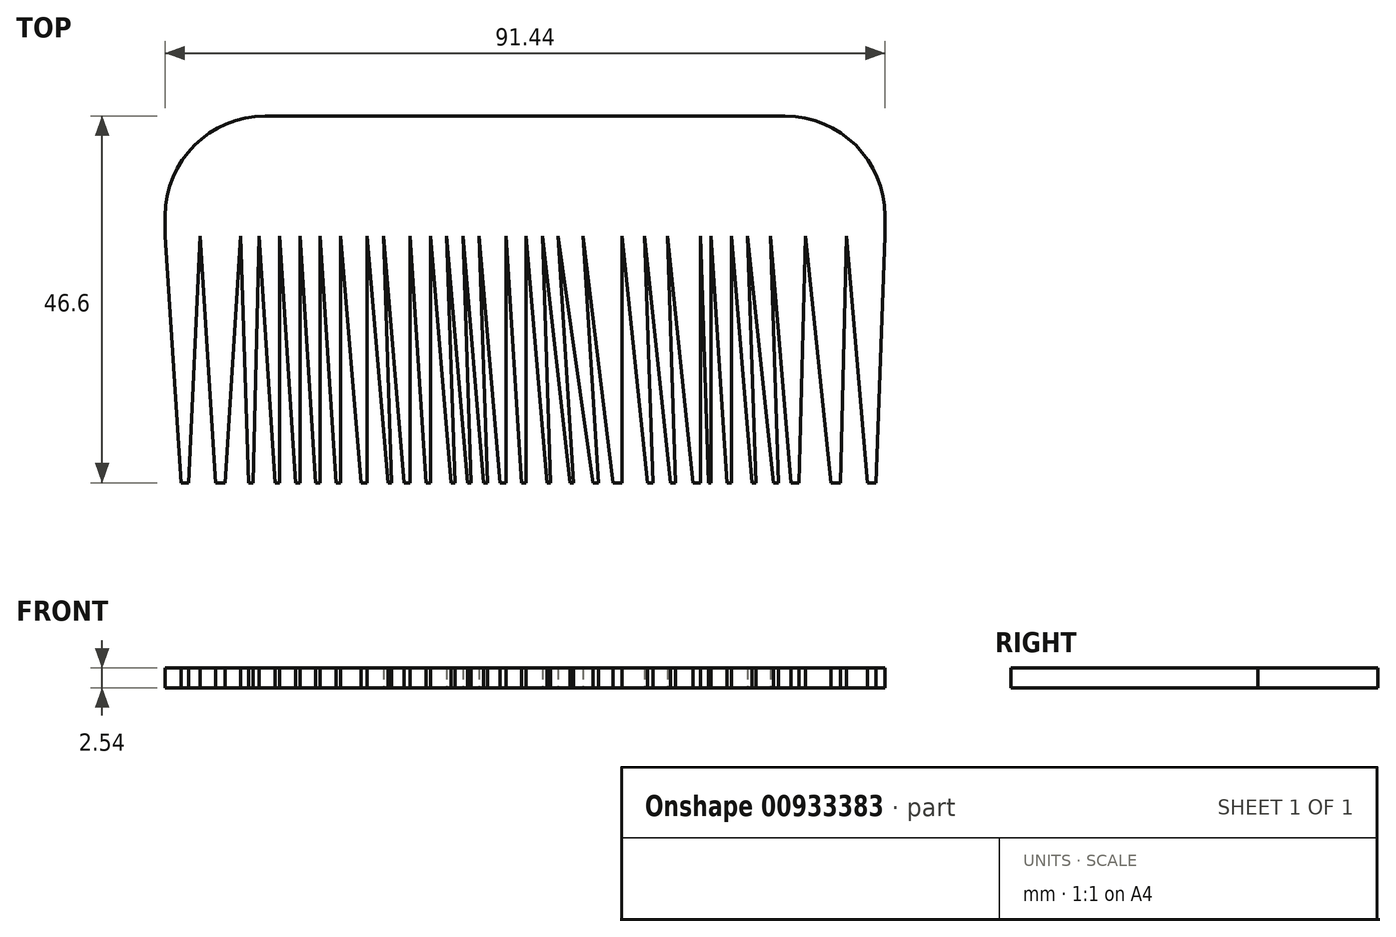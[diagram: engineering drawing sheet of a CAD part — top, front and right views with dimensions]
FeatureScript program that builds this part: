
annotation { "Feature Type Name" : "Feature", "Feature Type Description" : "" }
export const myFeature = defineFeature(function(context is Context, id is Id, definition is map)
    precondition{}
    {
        {
            var Q0;
            Q0=qCreatedBy(makeId("Top.planeOp"),FACE);
            var sketch = newSketch(context, id + "F0", { "sketchPlane" : qUnion([Q0])});
            skLineSegment(sketch, "E0.bottom", {"start": v(-18.06, 9.44) * mm, "end": v(73.38, 9.44) * mm});
            skLineSegment(sketch, "E0.top", {"start": v(-18.06, -5.8) * mm, "end": v(73.38, -5.8) * mm});
            skLineSegment(sketch, "E0.left", {"start": v(-18.06, 9.44) * mm, "end": v(-18.06, -5.8) * mm});
            skLineSegment(sketch, "E0.right", {"start": v(73.38, 9.44) * mm, "end": v(73.38, -5.8) * mm});
            skLineSegment(sketch, "E1", {"start": v(-18.06, -5.8) * mm, "end": v(-15.48, -46.4) * mm});
            skLineSegment(sketch, "E2", {"start": v(-15.48, -46.4) * mm, "end": v(73.76, -46.4) * mm});
            skLineSegment(sketch, "E3", {"start": v(-15.48, -46.4) * mm, "end": v(-13.62, -5.8) * mm});
            skLineSegment(sketch, "E4", {"start": v(-13.62, -5.8) * mm, "end": v(-11.04, -46.4) * mm});
            skLineSegment(sketch, "E5", {"start": v(-11.04, -46.4) * mm, "end": v(-8.47, -5.8) * mm});
            skLineSegment(sketch, "E6", {"start": v(-8.47, -5.8) * mm, "end": v(-7.13, -46.4) * mm});
            skLineSegment(sketch, "E7", {"start": v(-7.13, -46.4) * mm, "end": v(-6.1, -5.8) * mm});
            skLineSegment(sketch, "E8", {"start": v(-6.1, -5.8) * mm, "end": v(-3.52, -46.4) * mm});
            skLineSegment(sketch, "E9", {"start": v(-3.52, -46.4) * mm, "end": v(-3.52, -5.8) * mm});
            skLineSegment(sketch, "E10", {"start": v(-3.52, -5.8) * mm, "end": v(-0.94, -46.4) * mm});
            skLineSegment(sketch, "E11", {"start": v(-0.94, -46.4) * mm, "end": v(-0.94, -5.8) * mm});
            skLineSegment(sketch, "E12", {"start": v(-0.94, -5.8) * mm, "end": v(1.64, -46.4) * mm});
            skLineSegment(sketch, "E13", {"start": v(1.64, -46.4) * mm, "end": v(1.64, -5.8) * mm});
            skLineSegment(sketch, "E14", {"start": v(1.64, -5.8) * mm, "end": v(4.2, -46.2) * mm});
            skLineSegment(sketch, "E15", {"start": v(4.2, -46.2) * mm, "end": v(4.2, -5.8) * mm});
            skLineSegment(sketch, "E16", {"start": v(4.2, -5.8) * mm, "end": v(7.6, -46.4) * mm});
            skLineSegment(sketch, "E17", {"start": v(7.6, -46.4) * mm, "end": v(7.6, -5.8) * mm});
            skLineSegment(sketch, "E18", {"start": v(7.6, -5.8) * mm, "end": v(11, -46.4) * mm});
            skLineSegment(sketch, "E19", {"start": v(11, -46.4) * mm, "end": v(9.67, -5.8) * mm});
            skLineSegment(sketch, "E20", {"start": v(9.67, -5.8) * mm, "end": v(13.07, -46.4) * mm});
            skLineSegment(sketch, "E21", {"start": v(13.07, -46.4) * mm, "end": v(13.07, -5.8) * mm});
            skLineSegment(sketch, "E22", {"start": v(13.07, -5.8) * mm, "end": v(15.65, -46.4) * mm});
            skLineSegment(sketch, "E23", {"start": v(15.65, -46.4) * mm, "end": v(15.65, -5.8) * mm});
            skLineSegment(sketch, "E24", {"start": v(15.65, -5.8) * mm, "end": v(19.05, -46.4) * mm});
            skLineSegment(sketch, "E25", {"start": v(19.05, -46.4) * mm, "end": v(17.7, -5.8) * mm});
            skLineSegment(sketch, "E26", {"start": v(17.7, -5.8) * mm, "end": v(21.1, -46.4) * mm});
            skLineSegment(sketch, "E27", {"start": v(21.1, -46.4) * mm, "end": v(19.77, -5.8) * mm});
            skLineSegment(sketch, "E28", {"start": v(19.77, -5.8) * mm, "end": v(23.17, -46.4) * mm});
            skLineSegment(sketch, "E29", {"start": v(23.17, -46.4) * mm, "end": v(21.83, -5.8) * mm});
            skLineSegment(sketch, "E30", {"start": v(21.83, -5.8) * mm, "end": v(25.23, -46.4) * mm});
            skLineSegment(sketch, "E31", {"start": v(25.23, -46.4) * mm, "end": v(25.23, -5.8) * mm});
            skLineSegment(sketch, "E32", {"start": v(25.23, -5.8) * mm, "end": v(27.81, -46.4) * mm});
            skLineSegment(sketch, "E33", {"start": v(27.81, -46.4) * mm, "end": v(27.81, -5.8) * mm});
            skLineSegment(sketch, "E34", {"start": v(27.81, -5.8) * mm, "end": v(31.21, -46.4) * mm});
            skLineSegment(sketch, "E35", {"start": v(31.21, -46.4) * mm, "end": v(29.87, -5.8) * mm});
            skLineSegment(sketch, "E36", {"start": v(29.87, -5.8) * mm, "end": v(34.4, -46.4) * mm});
            skLineSegment(sketch, "E37", {"start": v(34.4, -46.4) * mm, "end": v(31.82, -5.8) * mm});
            skLineSegment(sketch, "E38", {"start": v(31.82, -5.8) * mm, "end": v(37.6, -46.4) * mm});
            skLineSegment(sketch, "E39", {"start": v(37.6, -46.4) * mm, "end": v(35.01, -5.8) * mm});
            skLineSegment(sketch, "E40", {"start": v(35.01, -5.8) * mm, "end": v(39.96, -46.4) * mm});
            skLineSegment(sketch, "E41", {"start": v(39.96, -46.4) * mm, "end": v(39.96, -5.8) * mm});
            skLineSegment(sketch, "E42", {"start": v(39.96, -5.8) * mm, "end": v(44.19, -46.4) * mm});
            skLineSegment(sketch, "E43", {"start": v(44.19, -46.4) * mm, "end": v(42.85, -5.8) * mm});
            skLineSegment(sketch, "E44", {"start": v(42.85, -5.8) * mm, "end": v(47.07, -46.4) * mm});
            skLineSegment(sketch, "E45", {"start": v(47.07, -46.4) * mm, "end": v(45.73, -5.8) * mm});
            skLineSegment(sketch, "E46", {"start": v(45.73, -5.8) * mm, "end": v(49.96, -46.4) * mm});
            skLineSegment(sketch, "E47", {"start": v(49.96, -46.4) * mm, "end": v(49.96, -5.8) * mm});
            skLineSegment(sketch, "E48", {"start": v(49.96, -5.8) * mm, "end": v(51.3, -46.4) * mm});
            skLineSegment(sketch, "E49", {"start": v(51.3, -46.4) * mm, "end": v(51.3, -5.8) * mm});
            skLineSegment(sketch, "E50", {"start": v(51.3, -5.8) * mm, "end": v(53.88, -46.4) * mm});
            skLineSegment(sketch, "E51", {"start": v(53.88, -46.4) * mm, "end": v(53.88, -5.8) * mm});
            skLineSegment(sketch, "E52", {"start": v(53.88, -5.8) * mm, "end": v(57.28, -46.4) * mm});
            skLineSegment(sketch, "E53", {"start": v(57.28, -46.4) * mm, "end": v(55.94, -5.8) * mm});
            skLineSegment(sketch, "E54", {"start": v(55.94, -5.8) * mm, "end": v(60.16, -46.4) * mm});
            skLineSegment(sketch, "E55", {"start": v(60.16, -46.4) * mm, "end": v(58.82, -5.8) * mm});
            skLineSegment(sketch, "E56", {"start": v(58.82, -5.8) * mm, "end": v(62.22, -46.4) * mm});
            skLineSegment(sketch, "E57", {"start": v(62.22, -46.4) * mm, "end": v(63.25, -5.8) * mm});
            skLineSegment(sketch, "E58", {"start": v(63.25, -5.8) * mm, "end": v(67.48, -46.4) * mm});
            skLineSegment(sketch, "E59", {"start": v(67.48, -46.4) * mm, "end": v(68.51, -5.8) * mm});
            skLineSegment(sketch, "E60", {"start": v(68.51, -5.8) * mm, "end": v(71.91, -46.4) * mm});
            skLineSegment(sketch, "E61", {"start": v(71.91, -46.4) * mm, "end": v(73.38, -5.8) * mm});
            skLineSegment(sketch, "E62", {"start": v(-16.06, -37.16) * mm, "end": v(72.25, -37.16) * mm});
            skSolve(sketch);
        }
        {
            var Q0;
            Q0=makeQuery(id+"F0.imprint","IMPRINT",FACE,{"disambiguationData":[TD([[makeQuery(id+"F0.imprint","IMPRINT",EDGE,{"derivedFrom":sQuery(id+"F0.wireOp",EDGE,"E0.bottom")}),-1.0]])]});
            var Q1;
            {var subQ0=sQuery(id+"F0.wireOp",EDGE,"E1");var subQ5=sQuery(id+"F0.wireOp",EDGE,"E62");var subQ6=makeQuery(id+"F0.imprint","INTERSECT",VERTEX,{"derivedFrom":[subQ0,subQ5]});Q1=makeQuery(id+"F0.imprint","IMPRINT",FACE,{"disambiguationData":[TD([[makeQuery(id+"F0.imprint","IMPRINT",EDGE,{"disambiguationData":[TD([[subQ6,-1.0]])],"derivedFrom":subQ5}),1.0]])]});}
            var Q2;
            {var subQ0=sQuery(id+"F0.wireOp",EDGE,"E4");var subQ5=sQuery(id+"F0.wireOp",EDGE,"E62");var subQ6=makeQuery(id+"F0.imprint","INTERSECT",VERTEX,{"derivedFrom":[subQ0,subQ5]});Q2=makeQuery(id+"F0.imprint","IMPRINT",FACE,{"disambiguationData":[TD([[makeQuery(id+"F0.imprint","IMPRINT",EDGE,{"disambiguationData":[TD([[subQ6,-1.0]])],"derivedFrom":subQ5}),1.0]])]});}
            var Q3;
            {var subQ0=sQuery(id+"F0.wireOp",EDGE,"E6");var subQ5=sQuery(id+"F0.wireOp",EDGE,"E62");var subQ6=makeQuery(id+"F0.imprint","INTERSECT",VERTEX,{"derivedFrom":[subQ0,subQ5]});Q3=makeQuery(id+"F0.imprint","IMPRINT",FACE,{"disambiguationData":[TD([[makeQuery(id+"F0.imprint","IMPRINT",EDGE,{"disambiguationData":[TD([[subQ6,-1.0]])],"derivedFrom":subQ5}),1.0]])]});}
            var Q4;
            {var subQ0=sQuery(id+"F0.wireOp",EDGE,"E8");var subQ5=sQuery(id+"F0.wireOp",EDGE,"E62");var subQ6=makeQuery(id+"F0.imprint","INTERSECT",VERTEX,{"derivedFrom":[subQ0,subQ5]});Q4=makeQuery(id+"F0.imprint","IMPRINT",FACE,{"disambiguationData":[TD([[makeQuery(id+"F0.imprint","IMPRINT",EDGE,{"disambiguationData":[TD([[subQ6,-1.0]])],"derivedFrom":subQ5}),1.0]])]});}
            var Q5;
            {var subQ0=sQuery(id+"F0.wireOp",EDGE,"E10");var subQ5=sQuery(id+"F0.wireOp",EDGE,"E62");var subQ7=makeQuery(id+"F0.imprint","INTERSECT",VERTEX,{"derivedFrom":[subQ0,subQ5]});Q5=makeQuery(id+"F0.imprint","IMPRINT",FACE,{"disambiguationData":[TD([[makeQuery(id+"F0.imprint","IMPRINT",EDGE,{"disambiguationData":[TD([[subQ7,-1.0]])],"derivedFrom":subQ5}),1.0]])]});}
            var Q6;
            {var subQ0=sQuery(id+"F0.wireOp",EDGE,"E12");var subQ5=sQuery(id+"F0.wireOp",EDGE,"E62");var subQ6=makeQuery(id+"F0.imprint","INTERSECT",VERTEX,{"derivedFrom":[subQ0,subQ5]});Q6=makeQuery(id+"F0.imprint","IMPRINT",FACE,{"disambiguationData":[TD([[makeQuery(id+"F0.imprint","IMPRINT",EDGE,{"disambiguationData":[TD([[subQ6,-1.0]])],"derivedFrom":subQ5}),1.0]])]});}
            var Q7;
            {var subQ0=sQuery(id+"F0.wireOp",EDGE,"E14");var subQ5=sQuery(id+"F0.wireOp",EDGE,"E62");var subQ6=makeQuery(id+"F0.imprint","INTERSECT",VERTEX,{"derivedFrom":[subQ0,subQ5]});Q7=makeQuery(id+"F0.imprint","IMPRINT",FACE,{"disambiguationData":[TD([[makeQuery(id+"F0.imprint","IMPRINT",EDGE,{"disambiguationData":[TD([[subQ6,-1.0]])],"derivedFrom":subQ5}),1.0]])]});}
            var Q8;
            {var subQ0=sQuery(id+"F0.wireOp",EDGE,"E16");var subQ5=sQuery(id+"F0.wireOp",EDGE,"E62");var subQ6=makeQuery(id+"F0.imprint","INTERSECT",VERTEX,{"derivedFrom":[subQ0,subQ5]});Q8=makeQuery(id+"F0.imprint","IMPRINT",FACE,{"disambiguationData":[TD([[makeQuery(id+"F0.imprint","IMPRINT",EDGE,{"disambiguationData":[TD([[subQ6,-1.0]])],"derivedFrom":subQ5}),1.0]])]});}
            var Q9;
            {var subQ0=sQuery(id+"F0.wireOp",EDGE,"E20");var subQ5=sQuery(id+"F0.wireOp",EDGE,"E62");var subQ7=makeQuery(id+"F0.imprint","INTERSECT",VERTEX,{"derivedFrom":[subQ0,subQ5]});Q9=makeQuery(id+"F0.imprint","IMPRINT",FACE,{"disambiguationData":[TD([[makeQuery(id+"F0.imprint","IMPRINT",EDGE,{"disambiguationData":[TD([[subQ7,-1.0]])],"derivedFrom":subQ5}),1.0]])]});}
            var Q10;
            {var subQ0=sQuery(id+"F0.wireOp",EDGE,"E22");var subQ5=sQuery(id+"F0.wireOp",EDGE,"E62");var subQ6=makeQuery(id+"F0.imprint","INTERSECT",VERTEX,{"derivedFrom":[subQ0,subQ5]});Q10=makeQuery(id+"F0.imprint","IMPRINT",FACE,{"disambiguationData":[TD([[makeQuery(id+"F0.imprint","IMPRINT",EDGE,{"disambiguationData":[TD([[subQ6,-1.0]])],"derivedFrom":subQ5}),1.0]])]});}
            var Q11;
            {var subQ0=sQuery(id+"F0.wireOp",EDGE,"E24");var subQ5=sQuery(id+"F0.wireOp",EDGE,"E62");var subQ6=makeQuery(id+"F0.imprint","INTERSECT",VERTEX,{"derivedFrom":[subQ0,subQ5]});Q11=makeQuery(id+"F0.imprint","IMPRINT",FACE,{"disambiguationData":[TD([[makeQuery(id+"F0.imprint","IMPRINT",EDGE,{"disambiguationData":[TD([[subQ6,-1.0]])],"derivedFrom":subQ5}),1.0]])]});}
            var Q12;
            {var subQ0=sQuery(id+"F0.wireOp",EDGE,"E26");var subQ5=sQuery(id+"F0.wireOp",EDGE,"E62");var subQ6=makeQuery(id+"F0.imprint","INTERSECT",VERTEX,{"derivedFrom":[subQ0,subQ5]});Q12=makeQuery(id+"F0.imprint","IMPRINT",FACE,{"disambiguationData":[TD([[makeQuery(id+"F0.imprint","IMPRINT",EDGE,{"disambiguationData":[TD([[subQ6,-1.0]])],"derivedFrom":subQ5}),1.0]])]});}
            var Q13;
            {var subQ0=sQuery(id+"F0.wireOp",EDGE,"E28");var subQ5=sQuery(id+"F0.wireOp",EDGE,"E62");var subQ6=makeQuery(id+"F0.imprint","INTERSECT",VERTEX,{"derivedFrom":[subQ0,subQ5]});Q13=makeQuery(id+"F0.imprint","IMPRINT",FACE,{"disambiguationData":[TD([[makeQuery(id+"F0.imprint","IMPRINT",EDGE,{"disambiguationData":[TD([[subQ6,-1.0]])],"derivedFrom":subQ5}),1.0]])]});}
            var Q14;
            {var subQ0=sQuery(id+"F0.wireOp",EDGE,"E34");var subQ5=sQuery(id+"F0.wireOp",EDGE,"E62");var subQ6=makeQuery(id+"F0.imprint","INTERSECT",VERTEX,{"derivedFrom":[subQ0,subQ5]});Q14=makeQuery(id+"F0.imprint","IMPRINT",FACE,{"disambiguationData":[TD([[makeQuery(id+"F0.imprint","IMPRINT",EDGE,{"disambiguationData":[TD([[subQ6,-1.0]])],"derivedFrom":subQ5}),1.0]])]});}
            var Q15;
            {var subQ0=sQuery(id+"F0.wireOp",EDGE,"E36");var subQ5=sQuery(id+"F0.wireOp",EDGE,"E62");var subQ6=makeQuery(id+"F0.imprint","INTERSECT",VERTEX,{"derivedFrom":[subQ0,subQ5]});Q15=makeQuery(id+"F0.imprint","IMPRINT",FACE,{"disambiguationData":[TD([[makeQuery(id+"F0.imprint","IMPRINT",EDGE,{"disambiguationData":[TD([[subQ6,-1.0]])],"derivedFrom":subQ5}),1.0]])]});}
            var Q16;
            {var subQ0=sQuery(id+"F0.wireOp",EDGE,"E38");var subQ5=sQuery(id+"F0.wireOp",EDGE,"E62");var subQ6=makeQuery(id+"F0.imprint","INTERSECT",VERTEX,{"derivedFrom":[subQ0,subQ5]});Q16=makeQuery(id+"F0.imprint","IMPRINT",FACE,{"disambiguationData":[TD([[makeQuery(id+"F0.imprint","IMPRINT",EDGE,{"disambiguationData":[TD([[subQ6,-1.0]])],"derivedFrom":subQ5}),1.0]])]});}
            var Q17;
            {var subQ0=sQuery(id+"F0.wireOp",EDGE,"E40");var subQ5=sQuery(id+"F0.wireOp",EDGE,"E62");var subQ7=makeQuery(id+"F0.imprint","INTERSECT",VERTEX,{"derivedFrom":[subQ0,subQ5]});Q17=makeQuery(id+"F0.imprint","IMPRINT",FACE,{"disambiguationData":[TD([[makeQuery(id+"F0.imprint","IMPRINT",EDGE,{"disambiguationData":[TD([[subQ7,-1.0]])],"derivedFrom":subQ5}),1.0]])]});}
            var Q18;
            {var subQ0=sQuery(id+"F0.wireOp",EDGE,"E30");var subQ5=sQuery(id+"F0.wireOp",EDGE,"E62");var subQ7=makeQuery(id+"F0.imprint","INTERSECT",VERTEX,{"derivedFrom":[subQ0,subQ5]});Q18=makeQuery(id+"F0.imprint","IMPRINT",FACE,{"disambiguationData":[TD([[makeQuery(id+"F0.imprint","IMPRINT",EDGE,{"disambiguationData":[TD([[subQ7,-1.0]])],"derivedFrom":subQ5}),1.0]])]});}
            var Q19;
            {var subQ0=sQuery(id+"F0.wireOp",EDGE,"E32");var subQ5=sQuery(id+"F0.wireOp",EDGE,"E62");var subQ6=makeQuery(id+"F0.imprint","INTERSECT",VERTEX,{"derivedFrom":[subQ0,subQ5]});Q19=makeQuery(id+"F0.imprint","IMPRINT",FACE,{"disambiguationData":[TD([[makeQuery(id+"F0.imprint","IMPRINT",EDGE,{"disambiguationData":[TD([[subQ6,-1.0]])],"derivedFrom":subQ5}),1.0]])]});}
            var Q20;
            {var subQ0=sQuery(id+"F0.wireOp",EDGE,"E42");var subQ5=sQuery(id+"F0.wireOp",EDGE,"E62");var subQ6=makeQuery(id+"F0.imprint","INTERSECT",VERTEX,{"derivedFrom":[subQ0,subQ5]});Q20=makeQuery(id+"F0.imprint","IMPRINT",FACE,{"disambiguationData":[TD([[makeQuery(id+"F0.imprint","IMPRINT",EDGE,{"disambiguationData":[TD([[subQ6,-1.0]])],"derivedFrom":subQ5}),1.0]])]});}
            var Q21;
            {var subQ0=sQuery(id+"F0.wireOp",EDGE,"E44");var subQ5=sQuery(id+"F0.wireOp",EDGE,"E62");var subQ6=makeQuery(id+"F0.imprint","INTERSECT",VERTEX,{"derivedFrom":[subQ0,subQ5]});Q21=makeQuery(id+"F0.imprint","IMPRINT",FACE,{"disambiguationData":[TD([[makeQuery(id+"F0.imprint","IMPRINT",EDGE,{"disambiguationData":[TD([[subQ6,-1.0]])],"derivedFrom":subQ5}),1.0]])]});}
            var Q22;
            {var subQ0=sQuery(id+"F0.wireOp",EDGE,"E46");var subQ5=sQuery(id+"F0.wireOp",EDGE,"E62");var subQ6=makeQuery(id+"F0.imprint","INTERSECT",VERTEX,{"derivedFrom":[subQ0,subQ5]});Q22=makeQuery(id+"F0.imprint","IMPRINT",FACE,{"disambiguationData":[TD([[makeQuery(id+"F0.imprint","IMPRINT",EDGE,{"disambiguationData":[TD([[subQ6,-1.0]])],"derivedFrom":subQ5}),1.0]])]});}
            var Q23;
            {var subQ0=sQuery(id+"F0.wireOp",EDGE,"E48");var subQ5=sQuery(id+"F0.wireOp",EDGE,"E62");var subQ6=makeQuery(id+"F0.imprint","INTERSECT",VERTEX,{"derivedFrom":[subQ0,subQ5]});Q23=makeQuery(id+"F0.imprint","IMPRINT",FACE,{"disambiguationData":[TD([[makeQuery(id+"F0.imprint","IMPRINT",EDGE,{"disambiguationData":[TD([[subQ6,-1.0]])],"derivedFrom":subQ5}),1.0]])]});}
            var Q24;
            {var subQ0=sQuery(id+"F0.wireOp",EDGE,"E50");var subQ5=sQuery(id+"F0.wireOp",EDGE,"E62");var subQ7=makeQuery(id+"F0.imprint","INTERSECT",VERTEX,{"derivedFrom":[subQ0,subQ5]});Q24=makeQuery(id+"F0.imprint","IMPRINT",FACE,{"disambiguationData":[TD([[makeQuery(id+"F0.imprint","IMPRINT",EDGE,{"disambiguationData":[TD([[subQ7,-1.0]])],"derivedFrom":subQ5}),1.0]])]});}
            var Q25;
            {var subQ0=sQuery(id+"F0.wireOp",EDGE,"E52");var subQ5=sQuery(id+"F0.wireOp",EDGE,"E62");var subQ6=makeQuery(id+"F0.imprint","INTERSECT",VERTEX,{"derivedFrom":[subQ0,subQ5]});Q25=makeQuery(id+"F0.imprint","IMPRINT",FACE,{"disambiguationData":[TD([[makeQuery(id+"F0.imprint","IMPRINT",EDGE,{"disambiguationData":[TD([[subQ6,-1.0]])],"derivedFrom":subQ5}),1.0]])]});}
            var Q26;
            {var subQ0=sQuery(id+"F0.wireOp",EDGE,"E54");var subQ5=sQuery(id+"F0.wireOp",EDGE,"E62");var subQ6=makeQuery(id+"F0.imprint","INTERSECT",VERTEX,{"derivedFrom":[subQ0,subQ5]});Q26=makeQuery(id+"F0.imprint","IMPRINT",FACE,{"disambiguationData":[TD([[makeQuery(id+"F0.imprint","IMPRINT",EDGE,{"disambiguationData":[TD([[subQ6,-1.0]])],"derivedFrom":subQ5}),1.0]])]});}
            var Q27;
            {var subQ0=sQuery(id+"F0.wireOp",EDGE,"E56");var subQ5=sQuery(id+"F0.wireOp",EDGE,"E62");var subQ6=makeQuery(id+"F0.imprint","INTERSECT",VERTEX,{"derivedFrom":[subQ0,subQ5]});Q27=makeQuery(id+"F0.imprint","IMPRINT",FACE,{"disambiguationData":[TD([[makeQuery(id+"F0.imprint","IMPRINT",EDGE,{"disambiguationData":[TD([[subQ6,-1.0]])],"derivedFrom":subQ5}),1.0]])]});}
            var Q28;
            {var subQ0=sQuery(id+"F0.wireOp",EDGE,"E58");var subQ5=sQuery(id+"F0.wireOp",EDGE,"E62");var subQ6=makeQuery(id+"F0.imprint","INTERSECT",VERTEX,{"derivedFrom":[subQ0,subQ5]});Q28=makeQuery(id+"F0.imprint","IMPRINT",FACE,{"disambiguationData":[TD([[makeQuery(id+"F0.imprint","IMPRINT",EDGE,{"disambiguationData":[TD([[subQ6,-1.0]])],"derivedFrom":subQ5}),1.0]])]});}
            var Q29;
            {var subQ0=sQuery(id+"F0.wireOp",EDGE,"E61");var subQ5=sQuery(id+"F0.wireOp",EDGE,"E62");var subQ6=makeQuery(id+"F0.imprint","INTERSECT",VERTEX,{"derivedFrom":[subQ0,subQ5]});Q29=makeQuery(id+"F0.imprint","IMPRINT",FACE,{"disambiguationData":[TD([[makeQuery(id+"F0.imprint","IMPRINT",EDGE,{"disambiguationData":[TD([[subQ6,1.0]])],"derivedFrom":subQ5}),1.0]])]});}
            var Q30;
            {var subQ0=sQuery(id+"F0.wireOp",EDGE,"E18");var subQ5=sQuery(id+"F0.wireOp",EDGE,"E62");var subQ6=makeQuery(id+"F0.imprint","INTERSECT",VERTEX,{"derivedFrom":[subQ0,subQ5]});Q30=makeQuery(id+"F0.imprint","IMPRINT",FACE,{"disambiguationData":[TD([[makeQuery(id+"F0.imprint","IMPRINT",EDGE,{"disambiguationData":[TD([[subQ6,-1.0]])],"derivedFrom":subQ5}),1.0]])]});}
            extrude(context, id + "F1", {"entities" : qUnion([Q0, Q1, Q2, Q3, Q4, Q5, Q6, Q7, Q8, Q9, Q10, Q11, Q12, Q13, Q14, Q15, Q16, Q17, Q18, Q19, Q20, Q21, Q22, Q23, Q24, Q25, Q26, Q27, Q28, Q29, Q30]), "depth" : 2.54 * mm, "offsetDistance" : 25.4 * mm});
        }
        {
            var Q0;
            Q0=makeQuery(id+"F1.opExtrude","SWEPT_EDGE",EDGE,{"disambiguationData":[OSD([sQuery(id+"F0.wireOp",EDGE,"E0.bottom"),sQuery(id+"F0.wireOp",EDGE,"E0.right")])]});
            var Q1;
            Q1=makeQuery(id+"F1.opExtrude","SWEPT_EDGE",EDGE,{"disambiguationData":[OSD([sQuery(id+"F0.wireOp",EDGE,"E0.bottom"),sQuery(id+"F0.wireOp",EDGE,"E0.left")])]});
            fillet(context, id + "F2", {"entities" : qUnion([Q0, Q1]), "radius" : 12.7 * mm, "tangentPropagation" : true, "allowEdgeOverflow" : false});
        }
    });
